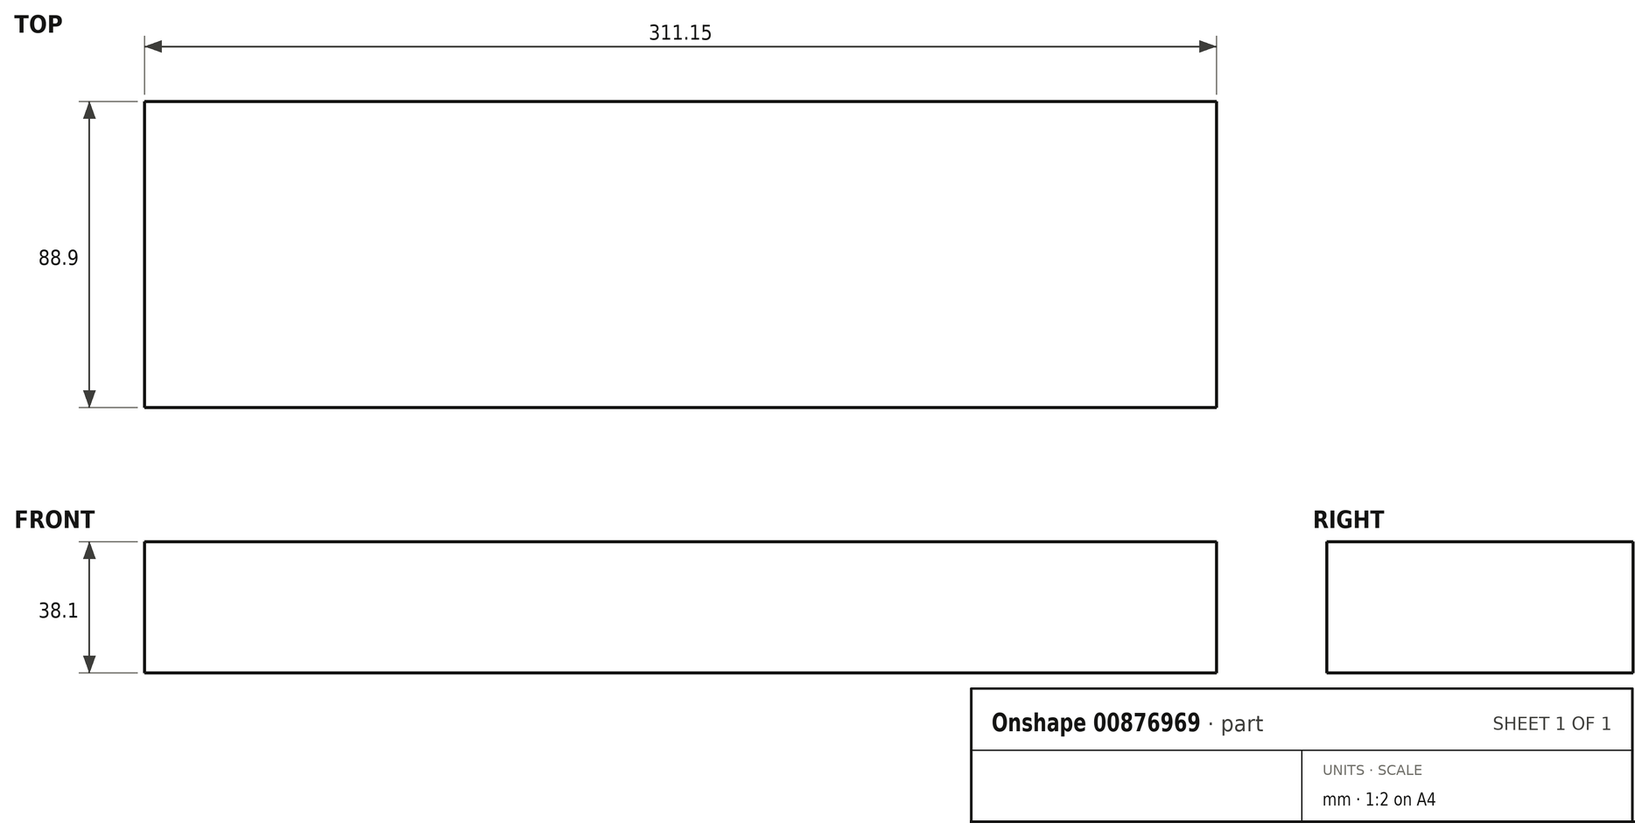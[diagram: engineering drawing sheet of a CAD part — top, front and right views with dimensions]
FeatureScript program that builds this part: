
annotation { "Feature Type Name" : "Feature", "Feature Type Description" : "" }
export const myFeature = defineFeature(function(context is Context, id is Id, definition is map)
    precondition{}
    {
        {
            var Q0;
            Q0=qCreatedBy(makeId("Right.planeOp"),FACE);
            var sketch = newSketch(context, id + "F0", { "sketchPlane" : qUnion([Q0])});
            skLineSegment(sketch, "E0.bottom", {"start": v(44.45, 19.05) * mm, "end": v(-44.45, 19.05) * mm});
            skLineSegment(sketch, "E0.top", {"start": v(44.45, -19.05) * mm, "end": v(-44.45, -19.05) * mm});
            skLineSegment(sketch, "E0.left", {"start": v(44.45, 19.05) * mm, "end": v(44.45, -19.05) * mm});
            skLineSegment(sketch, "E0.right", {"start": v(-44.45, 19.05) * mm, "end": v(-44.45, -19.05) * mm});
            skPoint(sketch, "E0.middle", {"position": v(0, 0) * mm});
            skSolve(sketch);
        }
        {
            var Q0;
            Q0=makeQuery(id+"F0.imprint","IMPRINT",FACE,{"disambiguationData":[TD([[makeQuery(id+"F0.imprint","IMPRINT",EDGE,{"derivedFrom":sQuery(id+"F0.wireOp",EDGE,"E0.bottom")}),1.0]])]});
            extrude(context, id + "F1", {"entities" : qUnion([Q0]), "depth" : 311.15 * mm, "offsetDistance" : 25.4 * mm});
        }
    });
